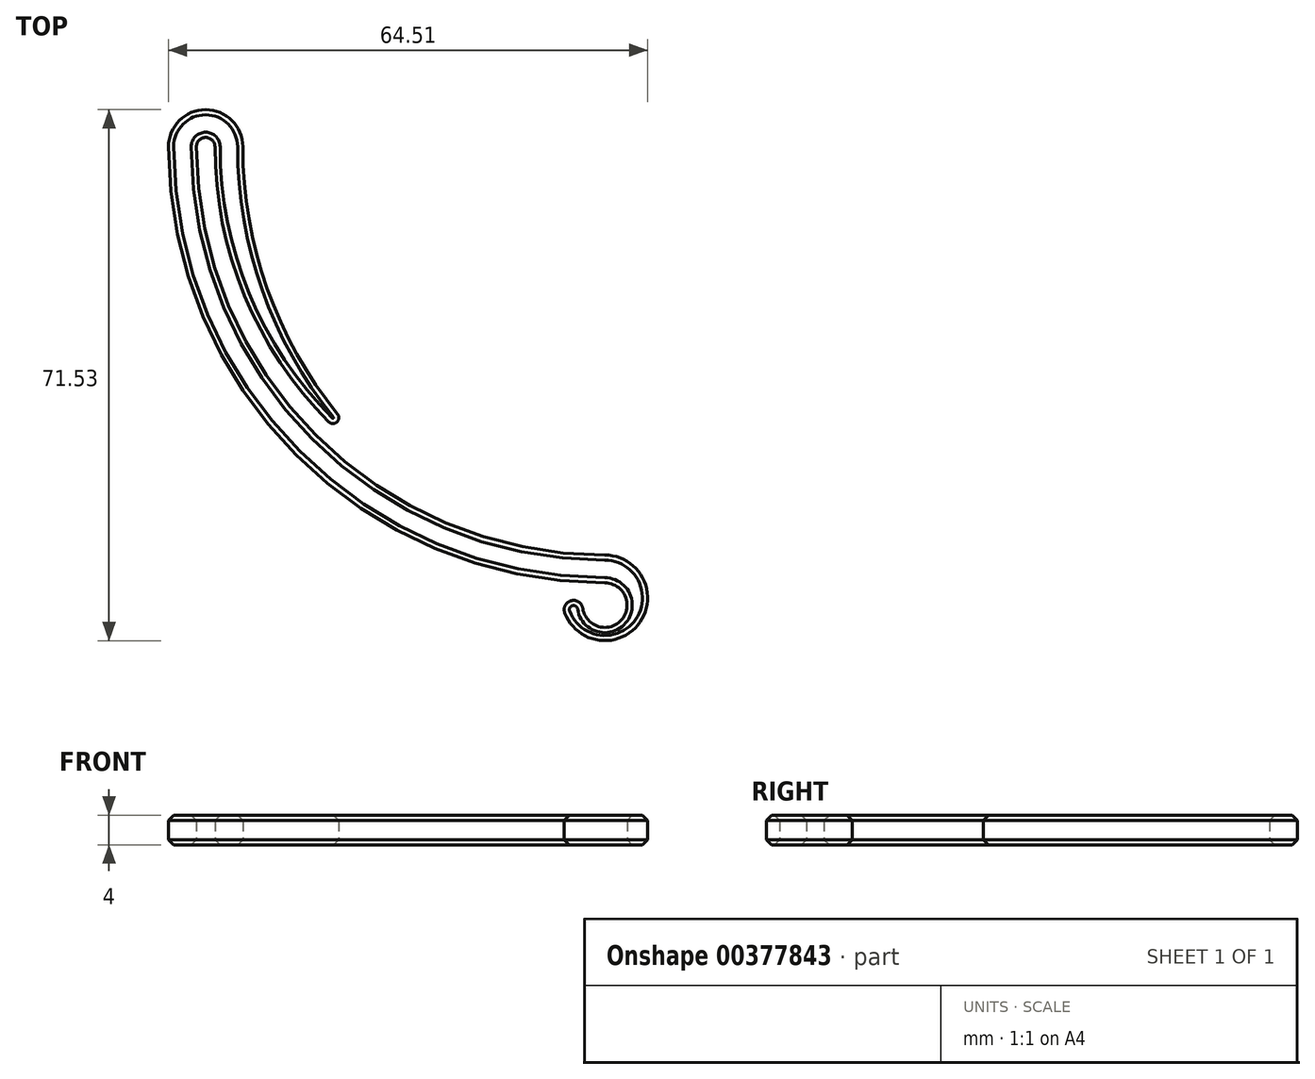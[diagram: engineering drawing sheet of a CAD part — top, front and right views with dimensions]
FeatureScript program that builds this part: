
annotation { "Feature Type Name" : "Feature", "Feature Type Description" : "" }
export const myFeature = defineFeature(function(context is Context, id is Id, definition is map)
    precondition{}
    {
        {
            var Q0;
            Q0=qCreatedBy(makeId("Top.planeOp"),FACE);
            var sketch = newSketch(context, id + "F0", { "sketchPlane" : qUnion([Q0])});
            skArc(sketch, "E0", {"start": v(-55, 0) * mm, "mid": v(-38.9, -38.9) * mm, "end": v(0, -55) * mm});
            skArc(sketch, "E1", {"start": v(-52.5, 0) * mm, "mid": v(-48.52, -20.05) * mm, "end": v(-37.18, -37.06) * mm});
            skArc(sketch, "E2", {"start": v(0, -55) * mm, "mid": v(4.75, -64.04) * mm, "end": v(-5.39, -62.81) * mm});
            skArc(sketch, "E3", {"start": v(-5.39, -62.81) * mm, "mid": v(-4.53, -61.15) * mm, "end": v(-2.97, -62.18) * mm});
            skArc(sketch, "E4", {"start": v(-37.18, -37.06) * mm, "mid": v(-36.08, -37.1) * mm, "end": v(-36, -36) * mm});
            skArc(sketch, "E5", {"start": v(-55, 0) * mm, "mid": v(-53.75, 1.25) * mm, "end": v(-52.5, 0) * mm});
            skLineSegment(sketch, "E6", {"start": v(-36, -36) * mm, "end": v(0, 0) * mm, "construction": true});
            skArc(sketch, "E7", {"start": v(-58.75, 0) * mm, "mid": v(-53.75, 5) * mm, "end": v(-48.75, 0) * mm});
            skLineSegment(sketch, "E8", {"start": v(-52.5, 0) * mm, "end": v(0, 0) * mm, "construction": true});
            skArc(sketch, "E9", {"start": v(-48.75, 0) * mm, "mid": v(-45.47, -19.1) * mm, "end": v(-36, -36) * mm});
            skArc(sketch, "E10", {"start": v(-58.75, 0) * mm, "mid": v(-41.54, -41.54) * mm, "end": v(0, -58.75) * mm});
            skArc(sketch, "E11", {"start": v(0, -58.75) * mm, "mid": v(2.27, -63.71) * mm, "end": v(-2.97, -62.18) * mm});
            skSolve(sketch);
        }
        {
            var Q0;
            Q0=makeQuery(id+"F0.imprint","IMPRINT",FACE,{"disambiguationData":[TD([[makeQuery(id+"F0.imprint","IMPRINT",EDGE,{"derivedFrom":sQuery(id+"F0.wireOp",EDGE,"E0")}),-1.0]])]});
            extrude(context, id + "F1", {"entities" : qUnion([Q0]), "depth" : 4 * mm});
        }
        {
            var Q0;
            Q0=makeQuery(id+"F1.opExtrude","CAP_EDGE",EDGE,{"disambiguationData":[OSD([sQuery(id+"F0.wireOp",EDGE,"E11")])],"isStart":false});
            var Q1;
            Q1=makeQuery(id+"F1.opExtrude","CAP_EDGE",EDGE,{"disambiguationData":[OSD([sQuery(id+"F0.wireOp",EDGE,"E11")])],"isStart":true});
            chamfer(context, id + "F2", {"entities" : qUnion([Q0, Q1]), "width" : 0.7 * mm, "tangentPropagation" : true});
        }
    });
